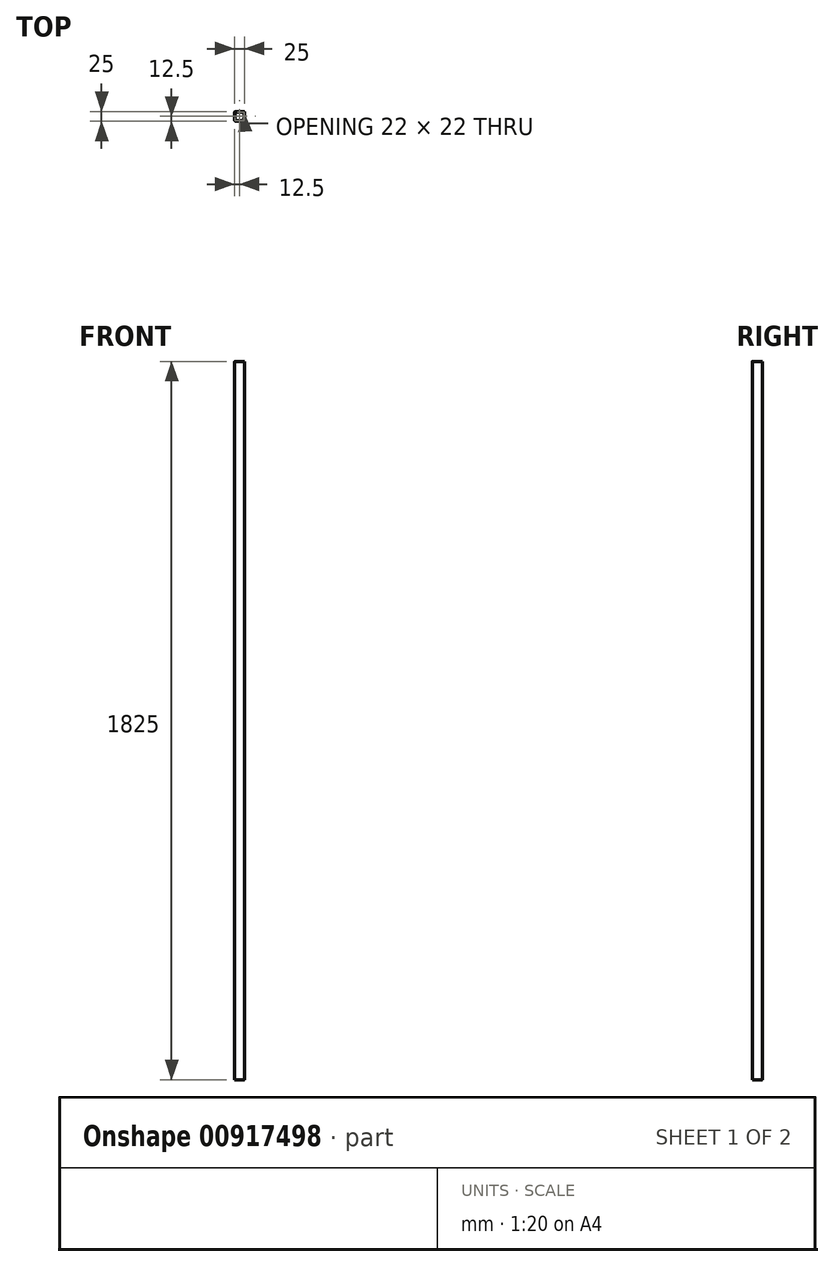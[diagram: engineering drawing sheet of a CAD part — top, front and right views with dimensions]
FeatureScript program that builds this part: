
annotation { "Feature Type Name" : "Feature", "Feature Type Description" : "" }
export const myFeature = defineFeature(function(context is Context, id is Id, definition is map)
    precondition{}
    {
        {
            var Q0;
            Q0=qCreatedBy(makeId("Top.planeOp"),FACE);
            var sketch = newSketch(context, id + "F0", { "sketchPlane" : qUnion([Q0])});
            skLineSegment(sketch, "E0.bottom", {"start": v(10, 12.5) * mm, "end": v(-10, 12.5) * mm});
            skLineSegment(sketch, "E0.top", {"start": v(10, -12.5) * mm, "end": v(-10, -12.5) * mm});
            skLineSegment(sketch, "E0.left", {"start": v(12.5, 10) * mm, "end": v(12.5, -10) * mm});
            skLineSegment(sketch, "E0.right", {"start": v(-12.5, 10) * mm, "end": v(-12.5, -10) * mm});
            skPoint(sketch, "E0.middle", {"position": v(0, 0) * mm});
            skPoint(sketch, "E1.visualSharp", {"position": v(-12.5, 12.5) * mm});
            skArc(sketch, "E1.filletArc", {"start": v(-10, 12.5) * mm, "mid": v(-11.77, 11.77) * mm, "end": v(-12.5, 10) * mm});
            skPoint(sketch, "E2.visualSharp", {"position": v(12.5, 12.5) * mm});
            skArc(sketch, "E2.filletArc", {"start": v(12.5, 10) * mm, "mid": v(11.77, 11.77) * mm, "end": v(10, 12.5) * mm});
            skPoint(sketch, "E3.visualSharp", {"position": v(12.5, -12.5) * mm});
            skArc(sketch, "E3.filletArc", {"start": v(10, -12.5) * mm, "mid": v(11.77, -11.77) * mm, "end": v(12.5, -10) * mm});
            skPoint(sketch, "E4.visualSharp", {"position": v(-12.5, -12.5) * mm});
            skArc(sketch, "E4.filletArc", {"start": v(-12.5, -10) * mm, "mid": v(-11.77, -11.77) * mm, "end": v(-10, -12.5) * mm});
            skLineSegment(sketch, "E5.0", {"start": v(10, -11) * mm, "end": v(-10, -11) * mm});
            skLineSegment(sketch, "E5.1", {"start": v(11, 11) * mm, "end": v(11, -10) * mm});
            skLineSegment(sketch, "E5.2", {"start": v(11, 11) * mm, "end": v(-10, 11) * mm});
            skLineSegment(sketch, "E5.3", {"start": v(-11, 10) * mm, "end": v(-11, -10) * mm});
            skPoint(sketch, "E6.visualSharp", {"position": v(-11, -11) * mm});
            skArc(sketch, "E6.filletArc", {"start": v(-11, -10) * mm, "mid": v(-10.7, -10.7) * mm, "end": v(-10, -11) * mm});
            skPoint(sketch, "E7.visualSharp", {"position": v(-11, 11) * mm});
            skArc(sketch, "E7.filletArc", {"start": v(-10, 11) * mm, "mid": v(-10.7, 10.7) * mm, "end": v(-11, 10) * mm});
            skPoint(sketch, "E8.visualSharp", {"position": v(11, -11) * mm});
            skArc(sketch, "E8.filletArc", {"start": v(10, -11) * mm, "mid": v(10.7, -10.7) * mm, "end": v(11, -10) * mm});
            skSolve(sketch);
        }
        {
            var Q0;
            Q0=qSketchRegion(id+"F0",true);
            extrude(context, id + "F1", {"entities" : qUnion([Q0]), "depth" : (2000 - 25 - 150) * mm, "offsetDistance" : 25 * mm});
        }
    });
